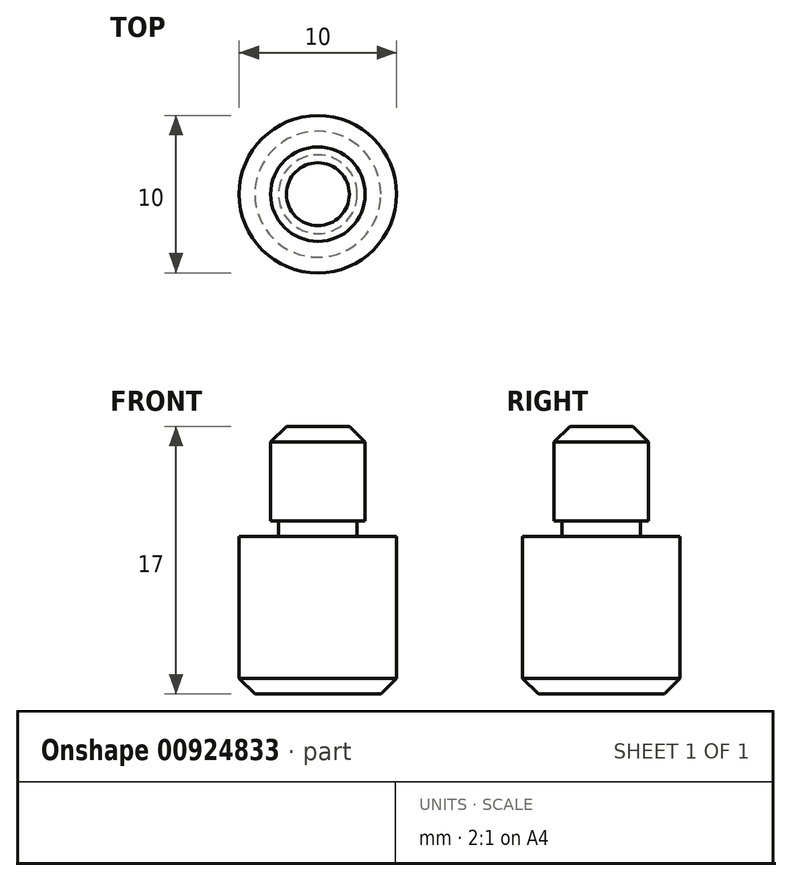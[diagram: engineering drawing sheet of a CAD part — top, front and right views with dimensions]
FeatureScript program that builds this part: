
annotation { "Feature Type Name" : "Feature", "Feature Type Description" : "" }
export const myFeature = defineFeature(function(context is Context, id is Id, definition is map)
    precondition{}
    {
        {
            var Q0;
            Q0=qCreatedBy(makeId("Top.planeOp"),FACE);
            var sketch = newSketch(context, id + "F0", { "sketchPlane" : qUnion([Q0])});
            skCircle(sketch, "E0", {"center": v(0, 0) * mm, "radius": 5 * mm});
            skSolve(sketch);
        }
        {
            var Q0;
            Q0 = qSketchRegion(id + "F0", true);
            extrude(context, id + "F1", {"entities" : qUnion([Q0]), "depth" : 10 * mm, "offsetDistance" : 25 * mm});
        }
        {
            var Q0;
            Q0=makeQuery(id+"F1.opExtrude","CAP_FACE",FACE,{"disambiguationData":[OSD([sQuery(id+"F0.wireOp",EDGE,"E0")])],"isStart":false});
            var sketch = newSketch(context, id + "F2", { "sketchPlane" : qUnion([Q0])});
            skCircle(sketch, "E1", {"center": v(0, 0) * mm, "radius": 3 * mm});
            skSolve(sketch);
        }
        {
            var Q0;
            Q0 = qSketchRegion(id + "F2", true);
            extrude(context, id + "F3", {"entities" : qUnion([Q0]), "operationType" : NewBodyOperationType.ADD, "depth" : 7 * mm, "offsetDistance" : 25 * mm});
        }
        {
            var Q0;
            Q0=qCreatedBy(makeId("Front.planeOp"),FACE);
            var sketch = newSketch(context, id + "F4", { "sketchPlane" : qUnion([Q0])});
            skLineSegment(sketch, "E2.bottom", {"start": v(3, 10) * mm, "end": v(2.5, 10) * mm});
            skLineSegment(sketch, "E2.top", {"start": v(3, 11) * mm, "end": v(2.5, 11) * mm});
            skLineSegment(sketch, "E2.left", {"start": v(3, 10) * mm, "end": v(3, 11) * mm});
            skLineSegment(sketch, "E2.right", {"start": v(2.5, 10) * mm, "end": v(2.5, 11) * mm});
            skSolve(sketch);
        }
        {
            var Q0;
            Q0 = qSketchRegion(id + "F4", true);
            var Q1;
            Q1=makeQuery(id+"F3.opExtrude","SWEPT_FACE",FACE,{"disambiguationData":[OSD([sQuery(id+"F2.wireOp",EDGE,"E1")])]});
            revolve(context, id + "F5", {"operationType" : NewBodyOperationType.REMOVE, "surfaceOperationType" : NewSurfaceOperationType.NEW, "entities" : qUnion([Q0]), "axis" : qUnion([Q1]), "revolveType" : RevolveType.FULL, "oppositeDirection" : true});
        }
        {
            var Q0;
            Q0=makeQuery(id+"F3.opExtrude","CAP_EDGE",EDGE,{"disambiguationData":[OSD([sQuery(id+"F2.wireOp",EDGE,"E1")])],"isStart":false});
            chamfer(context, id + "F6", {"entities" : qUnion([Q0]), "width" : 1 * mm, "tangentPropagation" : true});
        }
        {
            var Q0;
            Q0=makeQuery(id+"F1.opExtrude","CAP_EDGE",EDGE,{"disambiguationData":[OSD([sQuery(id+"F0.wireOp",EDGE,"E0")])],"isStart":true});
            chamfer(context, id + "F7", {"entities" : qUnion([Q0]), "width" : 1 * mm, "tangentPropagation" : true});
        }
    });
